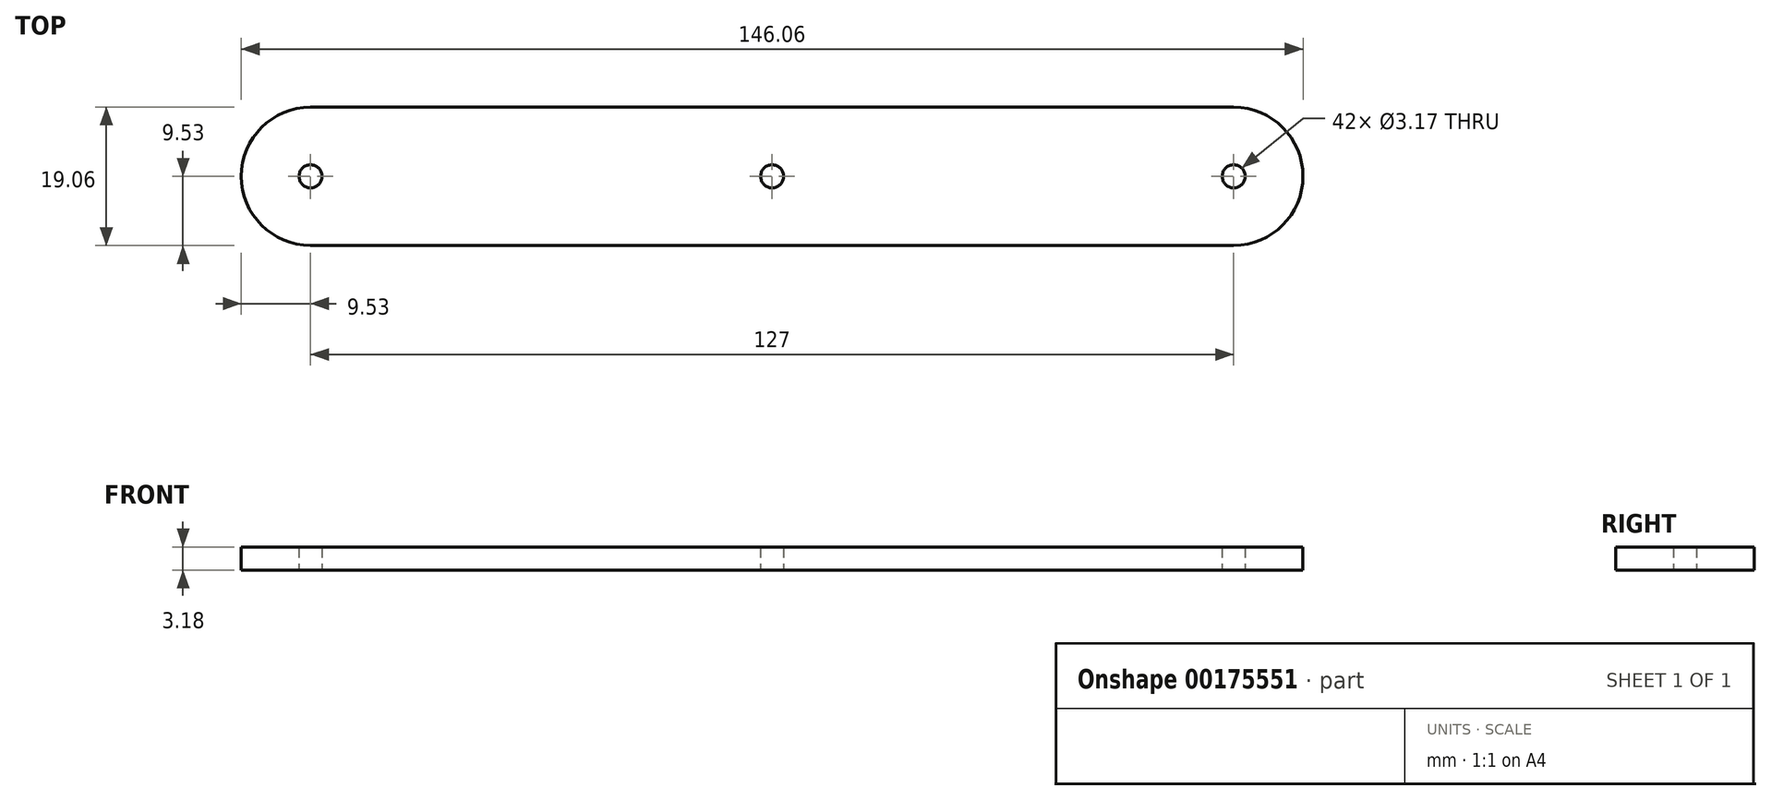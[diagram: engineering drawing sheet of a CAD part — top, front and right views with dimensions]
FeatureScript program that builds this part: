
annotation { "Feature Type Name" : "Feature", "Feature Type Description" : "" }
export const myFeature = defineFeature(function(context is Context, id is Id, definition is map)
    precondition{}
    {
        {
            var Q0;
            Q0=qCreatedBy(makeId("Top.planeOp"),FACE);
            var sketch = newSketch(context, id + "F0", { "sketchPlane" : qUnion([Q0])});
            skLineSegment(sketch, "E0.bottom", {"start": v(63.5, 9.53) * mm, "end": v(-63.5, 9.53) * mm});
            skLineSegment(sketch, "E0.top", {"start": v(63.5, -9.53) * mm, "end": v(-63.5, -9.53) * mm});
            skPoint(sketch, "E0.middle", {"position": v(0, 0) * mm});
            skArc(sketch, "E1", {"start": v(-63.5, 9.53) * mm, "mid": v(-73.03, 0) * mm, "end": v(-63.5, -9.53) * mm});
            skArc(sketch, "E2", {"start": v(63.5, -9.53) * mm, "mid": v(73.03, 0) * mm, "end": v(63.5, 9.53) * mm});
            skCircle(sketch, "E3", {"center": v(-63.5, 0) * mm, "radius": 1.59 * mm});
            skCircle(sketch, "E4", {"center": v(0, 0) * mm, "radius": 1.59 * mm});
            skCircle(sketch, "E5", {"center": v(63.5, 0) * mm, "radius": 1.59 * mm});
            skSolve(sketch);
        }
        {
            var Q0;
            Q0 = qSketchRegion(id + "F0", true);
            extrude(context, id + "F1", {"entities" : qUnion([Q0]), "depth" : 3.17 * mm});
        }
    });
